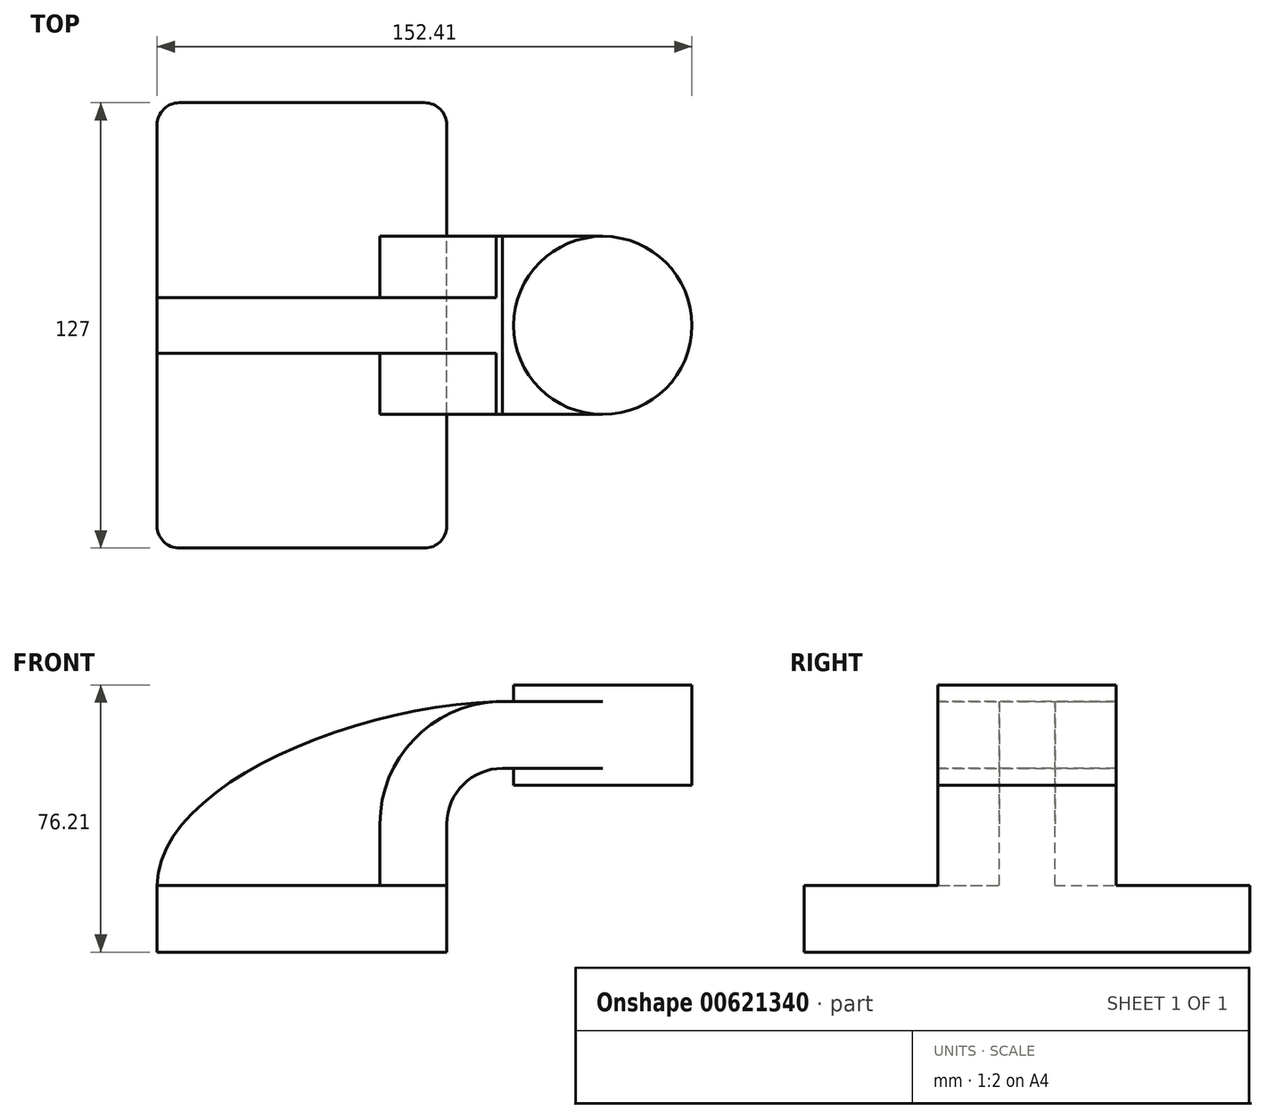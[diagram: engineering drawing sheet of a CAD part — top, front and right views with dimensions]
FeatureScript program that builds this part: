
annotation { "Feature Type Name" : "Feature", "Feature Type Description" : "" }
export const myFeature = defineFeature(function(context is Context, id is Id, definition is map)
    precondition{}
    {
        {
            var Q0;
            Q0=qCreatedBy(makeId("Front.planeOp"),FACE);
            var sketch = newSketch(context, id + "F0", { "sketchPlane" : qUnion([Q0])});
            skLineSegment(sketch, "E0.bottom", {"start": v(-41.28, 9.52) * mm, "end": v(41.27, 9.53) * mm});
            skLineSegment(sketch, "E0.top", {"start": v(-41.28, -9.53) * mm, "end": v(41.28, -9.53) * mm});
            skLineSegment(sketch, "E0.left", {"start": v(-41.28, 9.52) * mm, "end": v(-41.27, -9.53) * mm});
            skLineSegment(sketch, "E0.right", {"start": v(41.28, 9.53) * mm, "end": v(41.28, -9.52) * mm});
            skPoint(sketch, "E0.middle", {"position": v(0, 0) * mm});
            skLineSegment(sketch, "E1.bottom", {"start": v(60.32, 38.1) * mm, "end": v(111.12, 38.1) * mm});
            skLineSegment(sketch, "E1.top", {"start": v(60.32, 66.68) * mm, "end": v(111.12, 66.68) * mm});
            skLineSegment(sketch, "E1.left", {"start": v(60.32, 38.1) * mm, "end": v(60.32, 66.68) * mm});
            skLineSegment(sketch, "E1.right", {"start": v(111.12, 38.1) * mm, "end": v(111.12, 66.68) * mm});
            skPoint(sketch, "E1.middle", {"position": v(85.72, 52.39) * mm});
            skLineSegment(sketch, "E2", {"start": v(41.27, 9.53) * mm, "end": v(41.27, 27) * mm});
            skArc(sketch, "E3", {"start": v(41.27, 27) * mm, "mid": v(45.92, 38.23) * mm, "end": v(57.15, 42.88) * mm});
            skLineSegment(sketch, "E4", {"start": v(57.15, 42.88) * mm, "end": v(85.72, 42.88) * mm});
            skLineSegment(sketch, "E5.0", {"start": v(57.15, 61.93) * mm, "end": v(85.72, 61.93) * mm});
            skArc(sketch, "E5.1", {"start": v(22.22, 27) * mm, "mid": v(32.45, 51.7) * mm, "end": v(57.15, 61.93) * mm});
            skLineSegment(sketch, "E5.2", {"start": v(22.22, 9.53) * mm, "end": v(22.22, 27) * mm});
            skLineSegment(sketch, "E6", {"start": v(85.72, 38.1) * mm, "end": v(85.72, 66.68) * mm});
            skFitSpline(sketch, "E7", {"points": [v(-41.28, 9.53) * mm, v(57.15, 61.93) * mm], "startDerivative": vector(0.58, 83.86) * mm, "endDerivative": vector(130.07, 2.5) * mm});
            skSolve(sketch);
        }
        {
            var Q0;
            Q0=makeQuery(id+"F0.imprint","IMPRINT",FACE,{"disambiguationData":[TD([[makeQuery(id+"F0.imprint","IMPRINT",EDGE,{"derivedFrom":sQuery(id+"F0.wireOp",EDGE,"E0.top")}),1.0]])]});
            extrude(context, id + "F1", {"entities" : qUnion([Q0]), "endBound" : BoundingType.SYMMETRIC, "depth" : 127 * mm, "offsetDistance" : 25.4 * mm});
        }
        {
            var Q0;
            {var subQ1=sQuery(id+"F0.wireOp",EDGE,"E2");Q0=makeQuery(id+"F0.imprint","IMPRINT",FACE,{"disambiguationData":[TD([[makeQuery(id+"F0.imprint","IMPRINT",EDGE,{"derivedFrom":subQ1}),1.0]])]});}
            var Q1;
            {var subQ0=sQuery(id+"F0.wireOp",EDGE,"E4");var subQ1=sQuery(id+"F0.wireOp",EDGE,"E1.left");var subQ2=makeQuery(id+"F0.imprint","INTERSECT",VERTEX,{"derivedFrom":[subQ1,subQ0]});Q1=makeQuery(id+"F0.imprint","IMPRINT",FACE,{"disambiguationData":[TD([[makeQuery(id+"F0.imprint","IMPRINT",EDGE,{"disambiguationData":[TD([[subQ2,-1.0]])],"derivedFrom":subQ1}),-1.0]])]});}
            extrude(context, id + "F2", {"entities" : qUnion([Q0, Q1]), "operationType" : NewBodyOperationType.ADD, "endBound" : BoundingType.SYMMETRIC, "depth" : 50.8 * mm, "offsetDistance" : 25.4 * mm});
        }
        {
            var Q0;
            {var subQ3=sQuery(id+"F0.wireOp",EDGE,"E5.2");Q0=makeQuery(id+"F0.imprint","IMPRINT",FACE,{"disambiguationData":[TD([[makeQuery(id+"F0.imprint","IMPRINT",EDGE,{"derivedFrom":subQ3}),1.0]])]});}
            extrude(context, id + "F3", {"entities" : qUnion([Q0]), "operationType" : NewBodyOperationType.ADD, "endBound" : BoundingType.SYMMETRIC, "depth" : 15.88 * mm, "offsetDistance" : 25.4 * mm});
        }
        {
            var Q0;
            {var subQ4=sQuery(id+"F0.wireOp",EDGE,"E1.right");Q0=makeQuery(id+"F0.imprint","IMPRINT",FACE,{"disambiguationData":[TD([[makeQuery(id+"F0.imprint","IMPRINT",EDGE,{"derivedFrom":subQ4}),1.0]])]});}
            var Q1;
            Q1=sQuery(id+"F0.wireOp",EDGE,"E6");
            revolve(context, id + "F4", {"operationType" : NewBodyOperationType.ADD, "entities" : qUnion([Q0]), "axis" : qUnion([Q1]), "revolveType" : RevolveType.FULL});
        }
        {
            var Q0;
            Q0=makeQuery(id+"F1.opExtrude","CAP_EDGE",EDGE,{"disambiguationData":[OSD([sQuery(id+"F0.wireOp",EDGE,"E0.left")])],"isStart":false});
            var Q1;
            Q1=makeQuery(id+"F1.opExtrude","CAP_EDGE",EDGE,{"disambiguationData":[OSD([sQuery(id+"F0.wireOp",EDGE,"E0.right")])],"isStart":false});
            var Q2;
            Q2=makeQuery(id+"F1.opExtrude","CAP_EDGE",EDGE,{"disambiguationData":[OSD([sQuery(id+"F0.wireOp",EDGE,"E0.right")])],"isStart":true});
            var Q3;
            Q3=makeQuery(id+"F1.opExtrude","CAP_EDGE",EDGE,{"disambiguationData":[OSD([sQuery(id+"F0.wireOp",EDGE,"E0.left")])],"isStart":true});
            fillet(context, id + "F5", {"entities" : qUnion([Q0, Q1, Q2, Q3]), "radius" : 6.35 * mm, "tangentPropagation" : true, "allowEdgeOverflow" : false});
        }
    });
